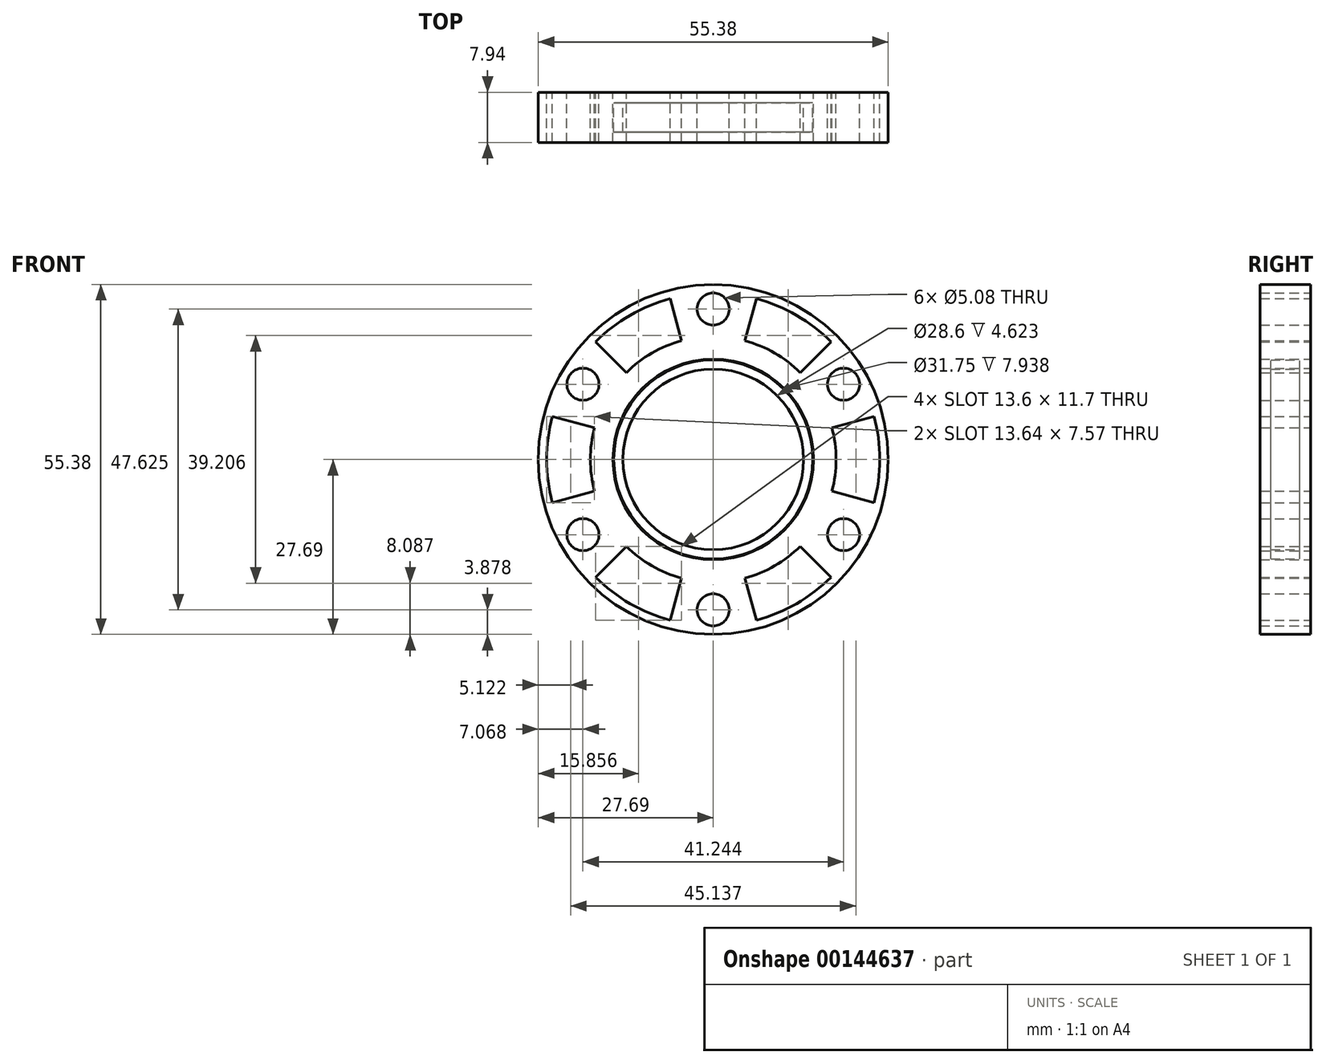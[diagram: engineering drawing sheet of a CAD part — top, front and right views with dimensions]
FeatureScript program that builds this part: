
annotation { "Feature Type Name" : "Feature", "Feature Type Description" : "" }
export const myFeature = defineFeature(function(context is Context, id is Id, definition is map)
    precondition{}
    {
        {
            var Q0;
            Q0=qCreatedBy(makeId("Front.planeOp"),FACE);
            var sketch = newSketch(context, id + "F0", { "sketchPlane" : qUnion([Q0])});
            skCircle(sketch, "E0", {"center": v(0, 0) * mm, "radius": 27.69 * mm});
            skCircle(sketch, "E1", {"center": v(0, 0) * mm, "radius": 19.45 * mm});
            skPoint(sketch, "E2", {"position": v(-18.78, 5.03) * mm});
            skPoint(sketch, "E3", {"position": v(-18.78, -5.03) * mm});
            skPoint(sketch, "E4", {"position": v(-26.74, 7.17) * mm});
            skPoint(sketch, "E5", {"position": v(-26.74, -7.17) * mm});
            skLineSegment(sketch, "E6", {"start": v(-18.78, 5.03) * mm, "end": v(-26.74, 7.17) * mm});
            skLineSegment(sketch, "E7", {"start": v(-18.78, -5.03) * mm, "end": v(-26.74, -7.17) * mm});
            skLineSegment(sketch, "E8.1.0", {"start": v(-5.03, -18.78) * mm, "end": v(-7.17, -26.74) * mm});
            skLineSegment(sketch, "E8.1.1", {"start": v(-13.75, -13.75) * mm, "end": v(-19.58, -19.58) * mm});
            skLineSegment(sketch, "E8.2.0", {"start": v(13.75, -13.75) * mm, "end": v(19.58, -19.58) * mm});
            skLineSegment(sketch, "E8.2.1", {"start": v(5.03, -18.78) * mm, "end": v(7.17, -26.74) * mm});
            skLineSegment(sketch, "E8.3.0", {"start": v(18.78, 5.03) * mm, "end": v(26.74, 7.17) * mm});
            skLineSegment(sketch, "E8.3.1", {"start": v(18.78, -5.03) * mm, "end": v(26.74, -7.17) * mm});
            skLineSegment(sketch, "E8.4.0", {"start": v(5.03, 18.78) * mm, "end": v(7.17, 26.74) * mm});
            skLineSegment(sketch, "E8.4.1", {"start": v(13.75, 13.75) * mm, "end": v(19.58, 19.58) * mm});
            skLineSegment(sketch, "E8.5.0", {"start": v(-13.75, 13.75) * mm, "end": v(-19.58, 19.58) * mm});
            skLineSegment(sketch, "E8.5.1", {"start": v(-5.03, 18.78) * mm, "end": v(-7.17, 26.74) * mm});
            skCircle(sketch, "E9", {"center": v(0, 0) * mm, "radius": 15.88 * mm});
            skCircle(sketch, "E10", {"center": v(0, 23.81) * mm, "radius": 2.54 * mm});
            skCircle(sketch, "E11.1.0", {"center": v(-20.62, 11.9) * mm, "radius": 2.54 * mm});
            skCircle(sketch, "E11.2.0", {"center": v(-20.62, -11.9) * mm, "radius": 2.54 * mm});
            skCircle(sketch, "E11.3.0", {"center": v(0, -23.81) * mm, "radius": 2.54 * mm});
            skCircle(sketch, "E11.4.0", {"center": v(20.62, -11.9) * mm, "radius": 2.54 * mm});
            skCircle(sketch, "E11.5.0", {"center": v(20.62, 11.9) * mm, "radius": 2.54 * mm});
            skCircle(sketch, "E12", {"center": v(0, 0) * mm, "radius": 26.35 * mm});
            skCircle(sketch, "E13", {"center": v(0, 0) * mm, "radius": 14.3 * mm});
            skCircle(sketch, "E14", {"center": v(0, 0) * mm, "radius": 15.75 * mm});
            skSolve(sketch);
        }
        {
            var Q0;
            {var subQ1=sQuery(id+"F0.wireOp",EDGE,"E0");var subQ5=sQuery(id+"F0.wireOp",EDGE,"E7");var subQ6=makeQuery(id+"F0.imprint","INTERSECT",VERTEX,{"derivedFrom":[subQ1,subQ5]});Q0=makeQuery(id+"F0.imprint","IMPRINT",FACE,{"disambiguationData":[TD([[makeQuery(id+"F0.imprint","IMPRINT",EDGE,{"disambiguationData":[TD([[subQ6,-1.0]])],"derivedFrom":subQ1}),1.0]])]});}
            var Q1;
            {var subQ0=sQuery(id+"F0.wireOp",EDGE,"E11.2.0");Q1=makeQuery(id+"F0.imprint","IMPRINT",FACE,{"disambiguationData":[TD([[makeQuery(id+"F0.imprint","IMPRINT",EDGE,{"derivedFrom":subQ0}),-1.0]])]});}
            var Q2;
            {var subQ0=sQuery(id+"F0.wireOp",EDGE,"E8.1.0");var subQ1=sQuery(id+"F0.wireOp",EDGE,"E0");var subQ2=makeQuery(id+"F0.imprint","INTERSECT",VERTEX,{"derivedFrom":[subQ1,subQ0]});Q2=makeQuery(id+"F0.imprint","IMPRINT",FACE,{"disambiguationData":[TD([[makeQuery(id+"F0.imprint","IMPRINT",EDGE,{"disambiguationData":[TD([[subQ2,1.0]])],"derivedFrom":subQ1}),1.0]])]});}
            var Q3;
            {var subQ2=sQuery(id+"F0.wireOp",EDGE,"E8.1.0");var subQ6=sQuery(id+"F0.wireOp",EDGE,"E0");var subQ8=makeQuery(id+"F0.imprint","INTERSECT",VERTEX,{"derivedFrom":[subQ6,subQ2]});Q3=makeQuery(id+"F0.imprint","IMPRINT",FACE,{"disambiguationData":[TD([[makeQuery(id+"F0.imprint","IMPRINT",EDGE,{"disambiguationData":[TD([[subQ8,-1.0]])],"derivedFrom":subQ6}),1.0]])]});}
            var Q4;
            {var subQ5=sQuery(id+"F0.wireOp",EDGE,"E11.3.0");Q4=makeQuery(id+"F0.imprint","IMPRINT",FACE,{"disambiguationData":[TD([[makeQuery(id+"F0.imprint","IMPRINT",EDGE,{"derivedFrom":subQ5}),-1.0]])]});}
            var Q5;
            {var subQ0=sQuery(id+"F0.wireOp",EDGE,"E8.2.0");var subQ1=sQuery(id+"F0.wireOp",EDGE,"E0");var subQ2=makeQuery(id+"F0.imprint","INTERSECT",VERTEX,{"derivedFrom":[subQ1,subQ0]});Q5=makeQuery(id+"F0.imprint","IMPRINT",FACE,{"disambiguationData":[TD([[makeQuery(id+"F0.imprint","IMPRINT",EDGE,{"disambiguationData":[TD([[subQ2,1.0]])],"derivedFrom":subQ1}),1.0]])]});}
            var Q6;
            {var subQ2=sQuery(id+"F0.wireOp",EDGE,"E8.2.0");var subQ5=sQuery(id+"F0.wireOp",EDGE,"E0");var subQ8=makeQuery(id+"F0.imprint","INTERSECT",VERTEX,{"derivedFrom":[subQ5,subQ2]});Q6=makeQuery(id+"F0.imprint","IMPRINT",FACE,{"disambiguationData":[TD([[makeQuery(id+"F0.imprint","IMPRINT",EDGE,{"disambiguationData":[TD([[subQ8,-1.0]])],"derivedFrom":subQ5}),1.0]])]});}
            var Q7;
            {var subQ0=sQuery(id+"F0.wireOp",EDGE,"E11.4.0");Q7=makeQuery(id+"F0.imprint","IMPRINT",FACE,{"disambiguationData":[TD([[makeQuery(id+"F0.imprint","IMPRINT",EDGE,{"derivedFrom":subQ0}),-1.0]])]});}
            var Q8;
            {var subQ0=sQuery(id+"F0.wireOp",EDGE,"E8.3.0");var subQ1=sQuery(id+"F0.wireOp",EDGE,"E0");var subQ2=makeQuery(id+"F0.imprint","INTERSECT",VERTEX,{"derivedFrom":[subQ1,subQ0]});Q8=makeQuery(id+"F0.imprint","IMPRINT",FACE,{"disambiguationData":[TD([[makeQuery(id+"F0.imprint","IMPRINT",EDGE,{"disambiguationData":[TD([[subQ2,1.0]])],"derivedFrom":subQ1}),1.0]])]});}
            var Q9;
            {var subQ0=sQuery(id+"F0.wireOp",EDGE,"E11.5.0");Q9=makeQuery(id+"F0.imprint","IMPRINT",FACE,{"disambiguationData":[TD([[makeQuery(id+"F0.imprint","IMPRINT",EDGE,{"derivedFrom":subQ0}),-1.0]])]});}
            var Q10;
            {var subQ1=sQuery(id+"F0.wireOp",EDGE,"E0");var subQ5=sQuery(id+"F0.wireOp",EDGE,"E8.3.0");var subQ6=makeQuery(id+"F0.imprint","INTERSECT",VERTEX,{"derivedFrom":[subQ1,subQ5]});Q10=makeQuery(id+"F0.imprint","IMPRINT",FACE,{"disambiguationData":[TD([[makeQuery(id+"F0.imprint","IMPRINT",EDGE,{"disambiguationData":[TD([[subQ6,-1.0]])],"derivedFrom":subQ1}),1.0]])]});}
            var Q11;
            {var subQ0=sQuery(id+"F0.wireOp",EDGE,"E8.4.0");var subQ1=sQuery(id+"F0.wireOp",EDGE,"E0");var subQ2=makeQuery(id+"F0.imprint","INTERSECT",VERTEX,{"derivedFrom":[subQ1,subQ0]});Q11=makeQuery(id+"F0.imprint","IMPRINT",FACE,{"disambiguationData":[TD([[makeQuery(id+"F0.imprint","IMPRINT",EDGE,{"disambiguationData":[TD([[subQ2,1.0]])],"derivedFrom":subQ1}),1.0]])]});}
            var Q12;
            {var subQ2=sQuery(id+"F0.wireOp",EDGE,"E8.4.0");var subQ5=sQuery(id+"F0.wireOp",EDGE,"E0");var subQ8=makeQuery(id+"F0.imprint","INTERSECT",VERTEX,{"derivedFrom":[subQ5,subQ2]});Q12=makeQuery(id+"F0.imprint","IMPRINT",FACE,{"disambiguationData":[TD([[makeQuery(id+"F0.imprint","IMPRINT",EDGE,{"disambiguationData":[TD([[subQ8,-1.0]])],"derivedFrom":subQ5}),1.0]])]});}
            var Q13;
            {var subQ0=sQuery(id+"F0.wireOp",EDGE,"E10");Q13=makeQuery(id+"F0.imprint","IMPRINT",FACE,{"disambiguationData":[TD([[makeQuery(id+"F0.imprint","IMPRINT",EDGE,{"derivedFrom":subQ0}),-1.0]])]});}
            var Q14;
            {var subQ0=sQuery(id+"F0.wireOp",EDGE,"E8.5.0");var subQ1=sQuery(id+"F0.wireOp",EDGE,"E0");var subQ2=makeQuery(id+"F0.imprint","INTERSECT",VERTEX,{"derivedFrom":[subQ1,subQ0]});Q14=makeQuery(id+"F0.imprint","IMPRINT",FACE,{"disambiguationData":[TD([[makeQuery(id+"F0.imprint","IMPRINT",EDGE,{"disambiguationData":[TD([[subQ2,1.0]])],"derivedFrom":subQ1}),1.0]])]});}
            var Q15;
            {var subQ4=sQuery(id+"F0.wireOp",EDGE,"E0");var subQ6=sQuery(id+"F0.wireOp",EDGE,"E6");var subQ7=makeQuery(id+"F0.imprint","INTERSECT",VERTEX,{"derivedFrom":[subQ4,subQ6]});Q15=makeQuery(id+"F0.imprint","IMPRINT",FACE,{"disambiguationData":[TD([[makeQuery(id+"F0.imprint","IMPRINT",EDGE,{"disambiguationData":[TD([[subQ7,1.0]])],"derivedFrom":subQ4}),1.0]])]});}
            var Q16;
            {var subQ0=sQuery(id+"F0.wireOp",EDGE,"E11.1.0");Q16=makeQuery(id+"F0.imprint","IMPRINT",FACE,{"disambiguationData":[TD([[makeQuery(id+"F0.imprint","IMPRINT",EDGE,{"derivedFrom":subQ0}),-1.0]])]});}
            var Q17;
            {var subQ0=sQuery(id+"F0.wireOp",EDGE,"E6");var subQ1=sQuery(id+"F0.wireOp",EDGE,"E0");var subQ2=makeQuery(id+"F0.imprint","INTERSECT",VERTEX,{"derivedFrom":[subQ1,subQ0]});Q17=makeQuery(id+"F0.imprint","IMPRINT",FACE,{"disambiguationData":[TD([[makeQuery(id+"F0.imprint","IMPRINT",EDGE,{"disambiguationData":[TD([[subQ2,-1.0]])],"derivedFrom":subQ1}),1.0]])]});}
            var Q18;
            Q18=makeQuery(id+"F0.imprint","IMPRINT",FACE,{"disambiguationData":[TD([[makeQuery(id+"F0.imprint","IMPRINT",EDGE,{"derivedFrom":sQuery(id+"F0.wireOp",EDGE,"E9")}),-1.0]])]});
            extrude(context, id + "F1", {"entities" : qUnion([Q0, Q1, Q2, Q3, Q4, Q5, Q6, Q7, Q8, Q9, Q10, Q11, Q12, Q13, Q14, Q15, Q16, Q17, Q18]), "endBound" : BoundingType.SYMMETRIC, "depth" : 7.94 * mm});
        }
        {
            var Q0;
            Q0=makeQuery(id+"F0.imprint","IMPRINT",FACE,{"disambiguationData":[TD([[makeQuery(id+"F0.imprint","IMPRINT",EDGE,{"derivedFrom":sQuery(id+"F0.wireOp",EDGE,"E13")}),-1.0]])]});
            extrude(context, id + "F2", {"entities" : qUnion([Q0]), "endBound" : BoundingType.SYMMETRIC, "depth" : 4.62 * mm});
        }
    });
